# Revit family: IS_Ceratherm_Multiproduct_BIM_GB_A5778;A5995
name_source: partatom
category: Plumbing Fixtures
revit_build: Autodesk Revit MEP 2012 (Build: 20110309_2315(x64)
units: mm (PartAtom-declared; Revit-internal decimal feet)

## types (2) — shared parameters
Accessories = www.idealspec.co.uk
AreaUnits = millimeters
Assembly Code = C1030200
AssetType = Fixed
BREEAMApproved = No
Brand = Ideal Standard
Color = Chrome
ConnectionType = Plumbing
Default Elevation = 1219 mm
DurationUnit = year
ECA = No
ExpectedLife = 30
FaucetFunction = MIXED
FaucetOperation = OTHER
FaucetType = OTHER
Features = Fixed round head and removable handset with dual bath filler
Finish = Chrome
FlowRateAt3Bar = 15.5 / 12 / 8 L min @ 2Bar
ISthermostatic = No
IfcExportAs = IfcValveType
IfcExportType = FAUCET
InstallationInstructions = www.idealspec.co.uk/resources.html
LinearUnits = millimeters
ManufacturerURL = www.idealspec.co.uk
Material = Brass
NBSDescription = Shower mixers
NBSReference = 45-35-70/335
NettWeight = 6.5 Kg
NominalHeight = 1051 mm  [stored 3.44816 ft]
NominalLength = 400 mm  [stored 1.31234 ft]
NominalWidth = 200 mm  [stored 0.656168 ft]
ShowerBody = ASH_ArmitageShanks_TapBody_Silver_render
Size = 1252 x 312 x 488 mm
Space = Internal
SpareParts = www.fastpart-spares.co.uk
TestPressure = 10 Bar
URL = www.idealspec.co.uk
Uniclass2 = Pr_40_20_87_81
Version = 2
VolumeUnits = Litres
WRAS = No
WarrantyDescription = Manufacturers Warranty
WarrantyDurationParts = 5
WarrantyDurationUnit = year
WaterEfficientProduct = Yes
WorkingPressure = 2 Bar
zero-valued in all types: CWFU, Cost, HWFU, WFU

## per-type parameters (varying)
| type | BIMObjectName | Description | Model | ModelNumber | ModelReference | Name | ProductInformation |
| A5778AA - Ceratherm 100 Dual Bath Shower Mixer Pack 1.6m | ISI_IdealStandard_ShowerMixers_Ceratherm_A5778AA | Ceratherm 100 Dual with Idealrain rainshower M1, fixed
riser 1.6m, M3 kit and Fastfix | A5778AA | A5778AA | Ceratherm 100 Dual with Idealrain rainshower M1, fixed
riser 1.6m, M3 kit and Fastfix | ShowerMixers_Ceratherm-A5778_IdealStandard | www.idealspec.co.uk/assets/datasheet/A5778AA |
| A5995AA - Ceratherm 100 Dual Bath Shower Mixer Pack 1.4m | ISI_IdealStandard_ShowerMixers_Ceratherm_A5995AA | Ceratherm 100 Dual with Idealrain rainshower M1, fixed
riser 1.4m, M3 kit and Fastfix
riser 1.4m, M3 kit and Fastfix | A5995AA | A5995AA | Ceratherm 100 Dual with Idealrain rainshower M1, fixed
riser 1.4m, M3 kit and Fastfix
riser 1.4m, M3 kit and Fastfix | ShowerMixers_Ceratherm-A5995_IdealStandard | www.idealspec.co.uk/assets/datasheet/A5995AA |

note: [stored X ft] marks values corroborated as IEEE doubles in the binary element streams (Revit-internal decimal feet)

## geometry (parser evidence)
native form markers: Sweep x5
no freeform markers — native parametric forms only
